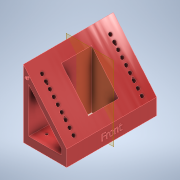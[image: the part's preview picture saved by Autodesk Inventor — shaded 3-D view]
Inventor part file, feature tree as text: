
AUTODESK INVENTOR PART (.ipt)
format: ipt  version: 2022.2 (Build 262287000, 287)  size: 572,416 bytes
history: native  units: mm
features: sketch x8, extrude x3, emboss x3, hole x2, mirror x1
ambient origin geometry x8: Origin, YZ Plane, XZ Plane, XY Plane, X Axis, Y Axis, Z Axis, Center Point
bodies: Body1 (feature_tree)
feature tree (17):
  extrude  "StartProfile"  Depth=6.981317mm
  sketch  "Sketch50"  dims[d225=125.0mm d226=166.0mm d227=0.0mm]
  sketch  "Sketch52"  dims[d228=126.0mm d229=34.0mm]
  extrude  "CutoutforAccessToBottomScrews"  Depth=166.0mm TaperAngle=0.0deg
  mirror  "Mirror3"
  hole  "HolesFor10-32ThruHoles"  [1 undecoded]
  hole  "Hole7"  [1 undecoded]
  extrude  "Extrusion24"  Depth=15.0mm
  emboss  "Emboss1"
  emboss  "Emboss2"
  emboss  "Emboss3"
  sketch  "Sketch49"  dims[d222=40.0mm d223=6.981317mm]
  sketch  "Sketch53"  dims[d230=20.0mm d231=23.0mm]
  sketch  "Sketch54"  dims[d232=20.0mm d234=126.0mm d235=90.0mm d237=11.333333mm d240=15.0mm]
  sketch  "Sketch55"  dims[d241=10.0mm]
  sketch  "Sketch56"  dims[d242=10.0mm]
  sketch  "Sketch57"  dims[d243=10.0mm d244=40.0mm d245=0.0mm d246=20.0mm d248=126.0mm d249=20.0mm d251=34.0mm d254=5.105mm d255=6.0mm d256=9.779mm d257=4.826mm d258=14.3117mm d259=8.0mm d260=0.0mm d261=5.812mm d262=6.0mm d263=6.582mm d264=7.41mm d265=90.0deg d266=10.0mm d267=0.0mm d268=15.0mm d269=15.0mm d270=0.0mm d271=0.0mm d272=1.0mm d273=0.0mm d274=1.0mm d275=0.0mm d276=20.0mm d277=1.0mm d278=0.0mm d64=1.0mm d65=1.0mm d66=1.0mm d67=0.15mm d68=0.25mm d69=0.375mm d70=14.3117mm d71=0.75mm d72=20.594885mm d73=0.0625mm d74=0.75mm d75=0.375mm]
note: 2 required parameter values undecoded (feature->parameter linkage not recoverable at this tier; creation-order binding heuristic only, values carry confidence <= 0.55)
